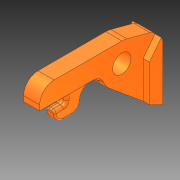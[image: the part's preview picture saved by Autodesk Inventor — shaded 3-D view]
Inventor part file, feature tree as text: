
AUTODESK INVENTOR PART (.ipt)
format: ipt  version: 2012 (Build 160160000, 160)  size: 202,752 bytes
history: native  units: mm
features: fillet x8, extrude x3, sketch x1
ambient origin geometry x8: Origin, YZ Plane, XZ Plane, XY Plane, X Axis, Y Axis, Z Axis, Center Point
bodies: Solid1 (feature_tree)
feature tree (12):
  sketch  "Sketch2"  dims[d9=10.0mm d10=0.0mm d11=5.6mm d12=0.0mm d16=13.6mm d17=28.5mm d18=4.6mm d19=12.0mm d22=75.0deg d23=15.0mm d29=1.0mm d30=6.0mm d57=8.0mm d58=9.0mm d59=4.0mm d60=4.0mm d61=13.0mm d62=6.4mm d63=3.8mm d64=1.0mm d65=3.0mm d66=0.0mm d67=3.0mm d68=3.0mm d69=1.0mm d70=1.0mm d71=0.5mm d72=5.0mm]
  extrude  "Extrusion1"  Depth=5.6mm TaperAngle=0.0deg
  extrude  "Extrusion2"  Depth=13.6mm
  extrude  "Extrusion6"  Depth=28.5mm
  fillet  "Fillet12"  Radius=4.6mm
  fillet  "Fillet11"  Radius=12.0mm
  fillet  "Fillet13"  [1 undecoded]
  fillet  "Fillet14"  Radius=15.0mm
  fillet  "Fillet15"  Radius=1.0mm
  fillet  "Fillet16"  Radius=6.0mm
  fillet  "Fillet17"  Radius=8.0mm
  fillet  "Fillet18"  Radius=9.0mm
note: 1 required parameter value undecoded (feature->parameter linkage not recoverable at this tier; creation-order binding heuristic only, values carry confidence <= 0.55)
